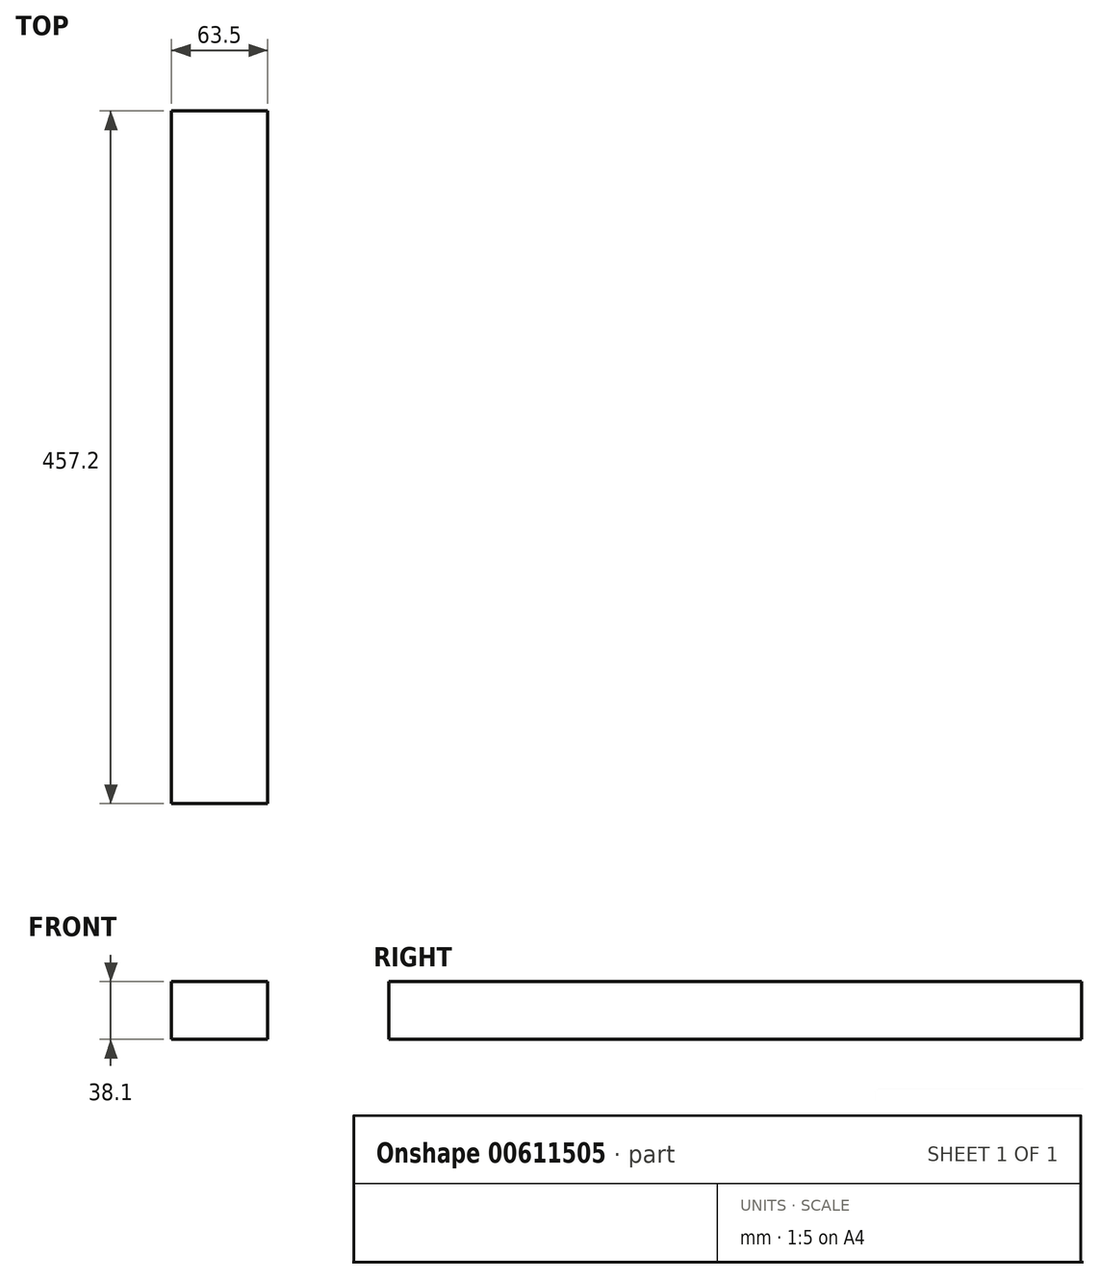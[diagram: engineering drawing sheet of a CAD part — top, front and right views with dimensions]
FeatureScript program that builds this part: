
annotation { "Feature Type Name" : "Feature", "Feature Type Description" : "" }
export const myFeature = defineFeature(function(context is Context, id is Id, definition is map)
    precondition{}
    {
        {
            var Q0;
            Q0=qCreatedBy(makeId("Front.planeOp"),FACE);
            var sketch = newSketch(context, id + "F0", { "sketchPlane" : qUnion([Q0])});
            skLineSegment(sketch, "E0.bottom", {"start": v(-24.66, 31.83) * mm, "end": v(38.84, 31.83) * mm});
            skLineSegment(sketch, "E0.top", {"start": v(-24.66, -6.27) * mm, "end": v(38.84, -6.27) * mm});
            skLineSegment(sketch, "E0.left", {"start": v(-24.66, 31.83) * mm, "end": v(-24.66, -6.27) * mm});
            skLineSegment(sketch, "E0.right", {"start": v(38.84, 31.83) * mm, "end": v(38.84, -6.27) * mm});
            skSolve(sketch);
        }
        {
            var Q0;
            Q0 = qSketchRegion(id + "F0", true);
            extrude(context, id + "F1", {"entities" : qUnion([Q0]), "depth" : 457.2 * mm, "offsetDistance" : 25.4 * mm});
        }
    });
